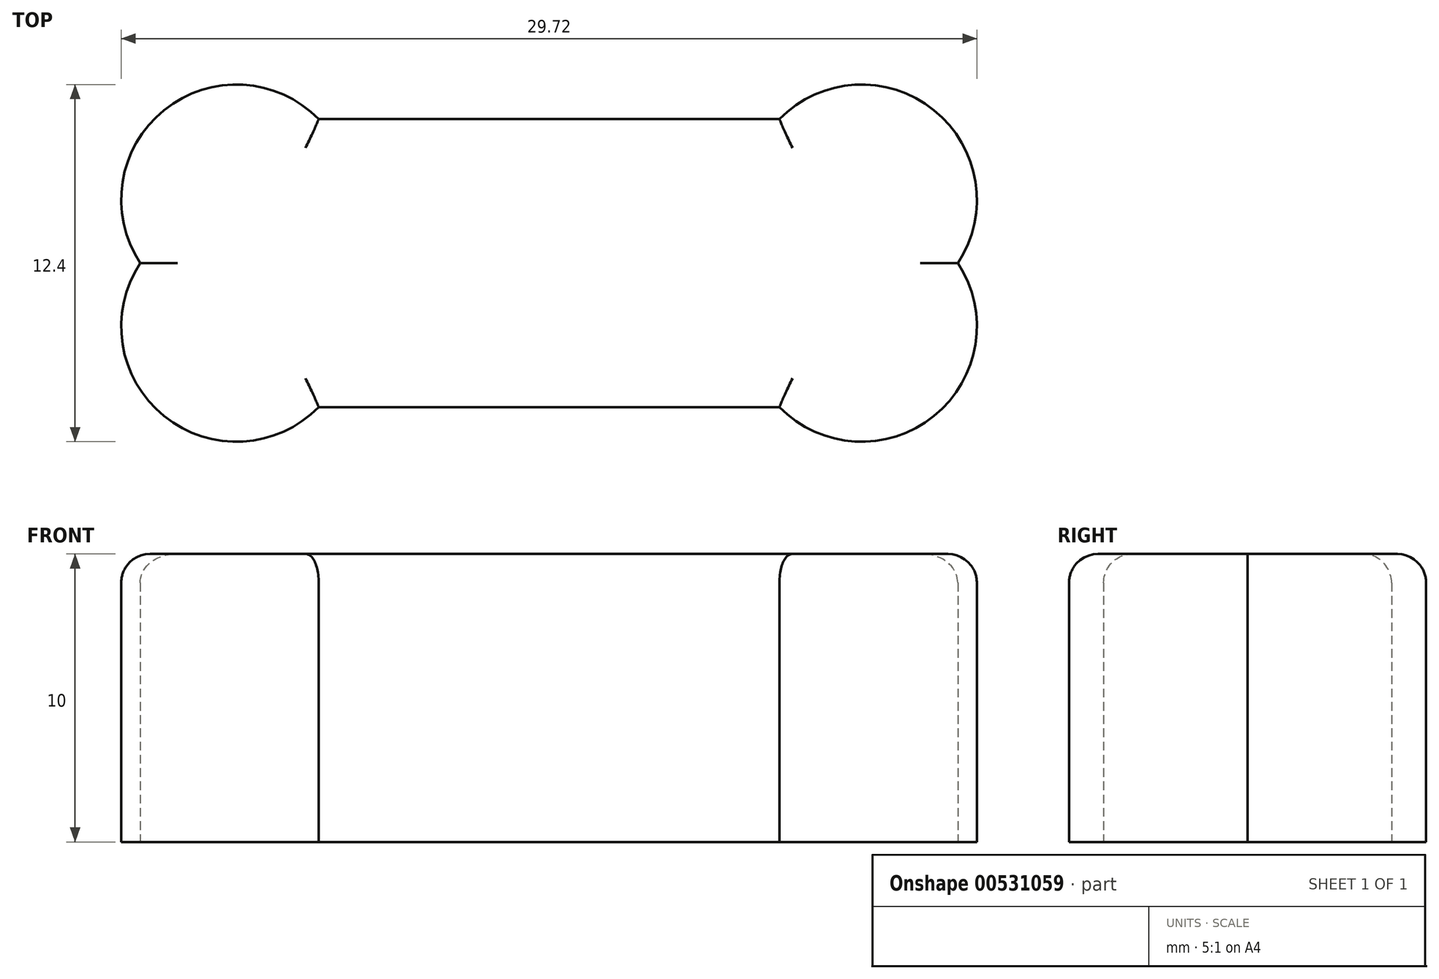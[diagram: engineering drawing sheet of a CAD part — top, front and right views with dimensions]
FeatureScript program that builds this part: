
annotation { "Feature Type Name" : "Feature", "Feature Type Description" : "" }
export const myFeature = defineFeature(function(context is Context, id is Id, definition is map)
    precondition{}
    {
        {
            var Q0;
            Q0=qCreatedBy(makeId("Top.planeOp"),FACE);
            var sketch = newSketch(context, id + "F0", { "sketchPlane" : qUnion([Q0])});
            skLineSegment(sketch, "E0", {"start": v(-8, 5) * mm, "end": v(0, 5) * mm});
            skLineSegment(sketch, "E1", {"start": v(-8, -5) * mm, "end": v(0, -5) * mm});
            skArc(sketch, "E2", {"start": v(-8, 5) * mm, "mid": v(-13.37, 5.31) * mm, "end": v(-14.2, 0) * mm});
            skArc(sketch, "E3", {"start": v(-14.2, 0) * mm, "mid": v(-13.37, -5.31) * mm, "end": v(-8, -5) * mm});
            skLineSegment(sketch, "E4.MirrorCS", {"start": v(8, 5) * mm, "end": v(0, 5) * mm});
            skArc(sketch, "E5.MirrorCS", {"start": v(8, 5) * mm, "mid": v(13.37, 5.31) * mm, "end": v(14.2, 0) * mm});
            skArc(sketch, "E6.MirrorCS", {"start": v(14.2, 0) * mm, "mid": v(13.37, -5.31) * mm, "end": v(8, -5) * mm});
            skLineSegment(sketch, "E7.MirrorCS", {"start": v(8, -5) * mm, "end": v(0, -5) * mm});
            skLineSegment(sketch, "E8", {"start": v(-8.2, 0) * mm, "end": v(3.55, 0) * mm});
            skSolve(sketch);
        }
        {
            var Q0;
            Q0=makeQuery(id+"F0.imprint","IMPRINT",FACE,{"disambiguationData":[TD([[makeQuery(id+"F0.imprint","IMPRINT",EDGE,{"derivedFrom":sQuery(id+"F0.wireOp",EDGE,"E0")}),-1.0]])]});
            extrude(context, id + "F1", {"entities" : qUnion([Q0]), "depth" : 10 * mm, "offsetDistance" : 25 * mm});
        }
        {
            var Q0;
            Q0=makeQuery(id+"F1.opExtrude","CAP_FACE",FACE,{"disambiguationData":[OSD([sQuery(id+"F0.wireOp",EDGE,"E0"),sQuery(id+"F0.wireOp",EDGE,"E1"),sQuery(id+"F0.wireOp",EDGE,"E2"),sQuery(id+"F0.wireOp",EDGE,"E3"),sQuery(id+"F0.wireOp",EDGE,"E4.MirrorCS"),sQuery(id+"F0.wireOp",EDGE,"E5.MirrorCS"),sQuery(id+"F0.wireOp",EDGE,"E6.MirrorCS"),sQuery(id+"F0.wireOp",EDGE,"E7.MirrorCS")])],"isStart":false});
            fillet(context, id + "F2", {"entities" : qUnion([Q0]), "radius" : 1 * mm, "tangentPropagation" : true, "allowEdgeOverflow" : false});
        }
    });
